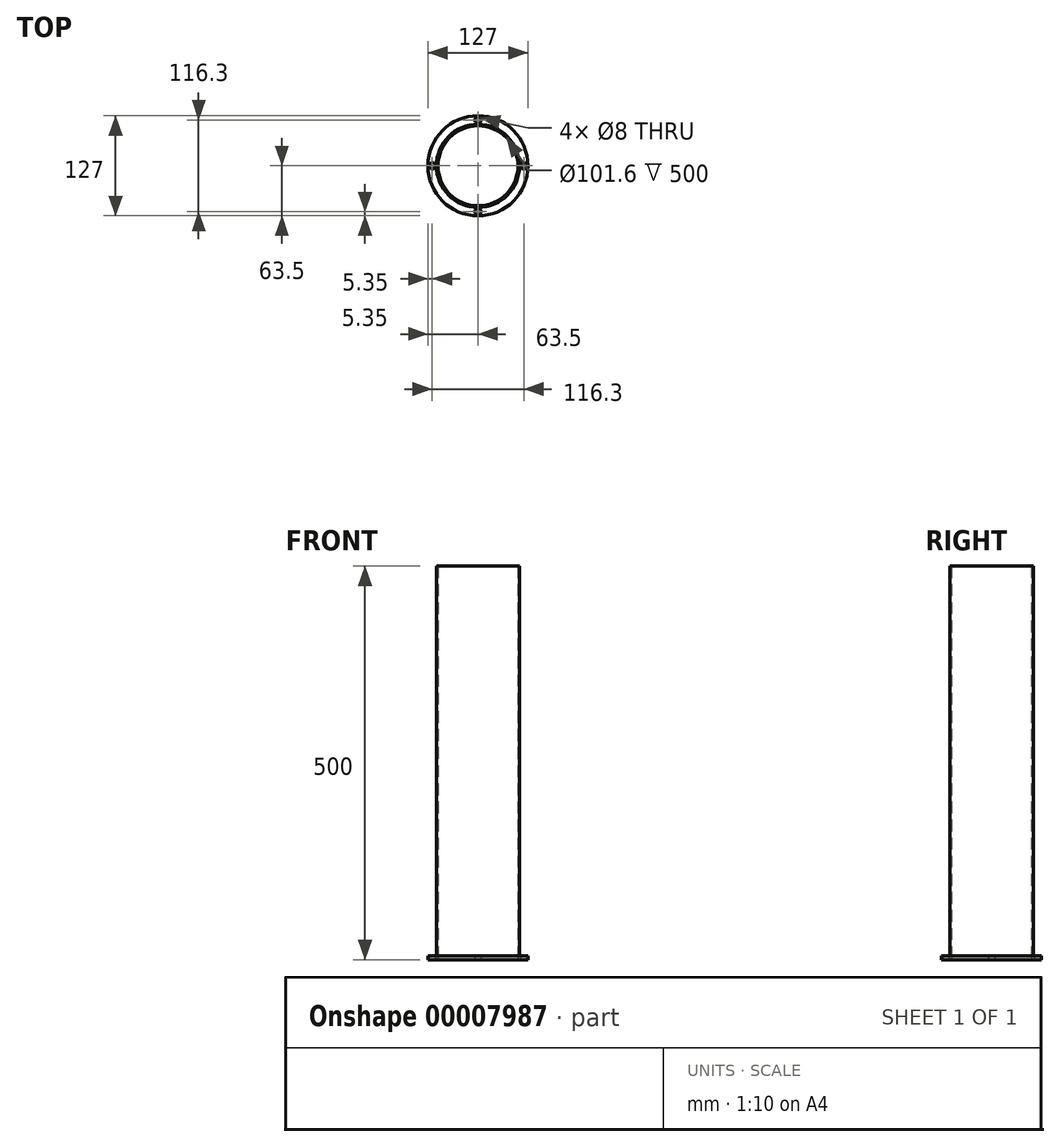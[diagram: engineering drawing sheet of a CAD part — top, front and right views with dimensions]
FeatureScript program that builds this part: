
annotation { "Feature Type Name" : "Feature", "Feature Type Description" : "" }
export const myFeature = defineFeature(function(context is Context, id is Id, definition is map)
    precondition{}
    {
        {
            var Q0;
            Q0=qCreatedBy(makeId("Top.planeOp"),FACE);
            var sketch = newSketch(context, id + "F0", { "sketchPlane" : qUnion([Q0])});
            skCircle(sketch, "E0", {"center": v(0, 0) * mm, "radius": 50.8 * mm});
            skCircle(sketch, "E1", {"center": v(0, 0) * mm, "radius": 52.8 * mm});
            skCircle(sketch, "E2", {"center": v(0, 0) * mm, "radius": 63.5 * mm});
            skCircle(sketch, "E3", {"center": v(0, 58.15) * mm, "radius": 4 * mm});
            skLineSegment(sketch, "E4", {"start": v(0, 63.5) * mm, "end": v(0, 52.8) * mm, "construction": true});
            skCircle(sketch, "E5.1.0", {"center": v(-58.15, 0) * mm, "radius": 4 * mm});
            skCircle(sketch, "E5.2.0", {"center": v(0, -58.15) * mm, "radius": 4 * mm});
            skCircle(sketch, "E6.1.3.0", {"center": v(58.15, 0) * mm, "radius": 4 * mm});
            skSolve(sketch);
        }
        {
            var Q0;
            Q0=makeQuery(id+"F0.imprint","IMPRINT",FACE,{"disambiguationData":[TD([[makeQuery(id+"F0.imprint","IMPRINT",EDGE,{"derivedFrom":sQuery(id+"F0.wireOp",EDGE,"E0")}),-1.0]])]});
            extrude(context, id + "F1", {"entities" : qUnion([Q0]), "depth" : 500 * mm});
        }
        {
            var Q0;
            Q0=makeQuery(id+"F0.imprint","IMPRINT",FACE,{"disambiguationData":[TD([[makeQuery(id+"F0.imprint","IMPRINT",EDGE,{"derivedFrom":sQuery(id+"F0.wireOp",EDGE,"E1")}),-1.0]])]});
            extrude(context, id + "F2", {"entities" : qUnion([Q0]), "operationType" : NewBodyOperationType.ADD, "depth" : 5 * mm});
        }
    });
